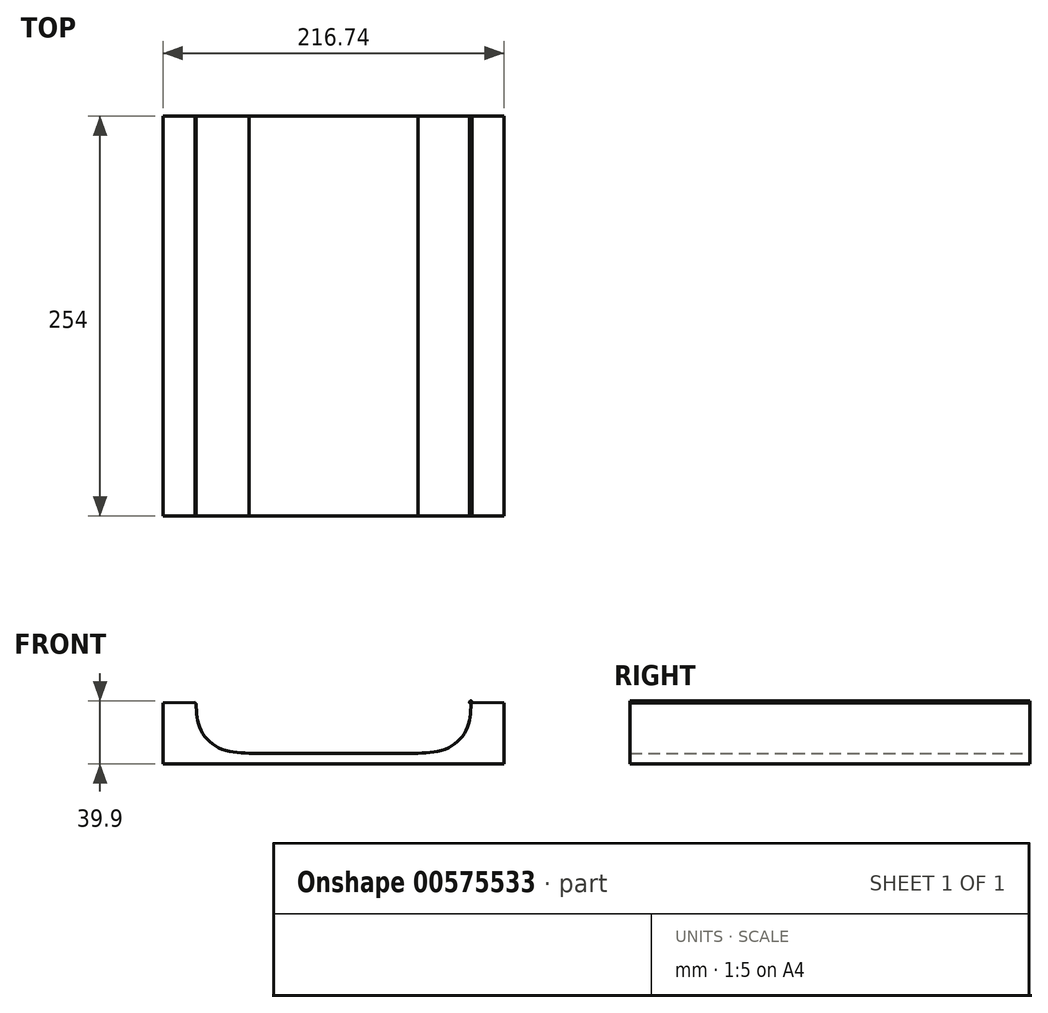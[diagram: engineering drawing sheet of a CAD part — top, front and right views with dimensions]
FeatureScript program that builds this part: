
annotation { "Feature Type Name" : "Feature", "Feature Type Description" : "" }
export const myFeature = defineFeature(function(context is Context, id is Id, definition is map)
    precondition{}
    {
        {
            var Q0;
            Q0=qCreatedBy(makeId("Front.planeOp"),FACE);
            var sketch = newSketch(context, id + "F0", { "sketchPlane" : qUnion([Q0])});
            skLineSegment(sketch, "E0.bottom", {"start": v(53.59, 3.32) * mm, "end": v(-53.59, 3.32) * mm});
            skLineSegment(sketch, "E0.top", {"start": v(53.59, -3.32) * mm, "end": v(-53.59, -3.32) * mm});
            skLineSegment(sketch, "E0.left", {"start": v(53.59, 3.32) * mm, "end": v(53.59, -3.32) * mm});
            skLineSegment(sketch, "E0.right", {"start": v(-53.59, 3.32) * mm, "end": v(-53.59, -3.32) * mm});
            skPoint(sketch, "E0.middle", {"position": v(0, 0) * mm});
            skFitSpline(sketch, "E1", {"points": [v(-53.59, 3.32) * mm, v(-73.74, 7.25) * mm, v(-85.05, 20.03) * mm, v(-87.26, 35.76) * mm], "startDerivative": vector(-60.33, 3.9) * mm, "endDerivative": vector(-1.15, 50.99) * mm});
            skFitSpline(sketch, "E2.MirrorCS", {"points": [v(53.59, 3.32) * mm, v(73.74, 7.25) * mm, v(85.05, 20.03) * mm, v(87.26, 35.76) * mm], "startDerivative": vector(60.33, 3.9) * mm, "endDerivative": vector(1.15, 50.99) * mm});
            skFitSpline(sketch, "E3.0", {"points": [v(54, -3.02) * mm, v(55.25, -2.94) * mm, v(57.81, -2.77) * mm, v(61.75, -2.43) * mm, v(65.75, -1.9) * mm, v(69.11, -1.2) * mm, v(71.8, -0.42) * mm, v(73.8, 0.29) * mm, v(75.78, 1.14) * mm, v(77.73, 2.16) * mm, v(79.56, 3.32) * mm, v(81.87, 5.02) * mm, v(84.48, 7.42) * mm, v(86.72, 10.1) * mm, v(88.27, 12.39) * mm, v(89.32, 14.16) * mm, v(90.1, 15.68) * mm, v(90.64, 16.93) * mm, v(91.16, 18.19) * mm, v(91.7, 19.77) * mm, v(92.4, 22.28) * mm, v(93, 25.37) * mm, v(93.5, 30.14) * mm, v(93.56, 33.5) * mm, v(93.6, 35.62) * mm]});
            skFitSpline(sketch, "E4.MirrorCS", {"points": [v(-53.59, 3.32) * mm, v(-73.74, 7.25) * mm, v(-85.05, 20.03) * mm, v(-87.26, 35.76) * mm], "startDerivative": vector(-60.33, 3.9) * mm, "endDerivative": vector(-1.15, 50.99) * mm});
            skFitSpline(sketch, "E5.0", {"points": [v(-54, -3.02) * mm, v(-55.25, -2.94) * mm, v(-57.81, -2.77) * mm, v(-61.75, -2.43) * mm, v(-65.75, -1.9) * mm, v(-69.11, -1.2) * mm, v(-71.8, -0.42) * mm, v(-73.8, 0.29) * mm, v(-75.78, 1.14) * mm, v(-77.73, 2.16) * mm, v(-79.56, 3.32) * mm, v(-81.87, 5.02) * mm, v(-84.48, 7.42) * mm, v(-86.72, 10.1) * mm, v(-88.27, 12.39) * mm, v(-89.32, 14.16) * mm, v(-90.1, 15.68) * mm, v(-90.64, 16.93) * mm, v(-91.16, 18.19) * mm, v(-91.7, 19.77) * mm, v(-92.4, 22.28) * mm, v(-93, 25.37) * mm, v(-93.5, 30.14) * mm, v(-93.56, 33.5) * mm, v(-93.6, 35.62) * mm]});
            skLineSegment(sketch, "E6", {"start": v(-93.6, 35.62) * mm, "end": v(-87.26, 35.76) * mm});
            skLineSegment(sketch, "E7", {"start": v(87.26, 35.76) * mm, "end": v(93.6, 35.62) * mm});
            skCircle(sketch, "E8", {"center": v(-87.26, 35.76) * mm, "radius": 0.81 * mm});
            skCircle(sketch, "E9.MirrorC", {"center": v(87.26, 35.76) * mm, "radius": 0.81 * mm});
            skLineSegment(sketch, "E10", {"start": v(-93.6, 35.62) * mm, "end": v(-109.54, 35.26) * mm});
            skLineSegment(sketch, "E11", {"start": v(-53.59, -3.32) * mm, "end": v(-108.37, -3.32) * mm});
            skLineSegment(sketch, "E12", {"start": v(-108.37, -3.32) * mm, "end": v(-108.37, 35.29) * mm});
            skLineSegment(sketch, "E13.MirrorCS", {"start": v(93.6, 35.62) * mm, "end": v(109.54, 35.26) * mm});
            skLineSegment(sketch, "E14.MirrorCS", {"start": v(108.37, -3.32) * mm, "end": v(108.37, 35.29) * mm});
            skLineSegment(sketch, "E15.MirrorCS", {"start": v(53.59, -3.32) * mm, "end": v(108.37, -3.32) * mm});
            skSolve(sketch);
        }
        {
            var Q0;
            {var subQ5=sQuery(id+"F0.wireOp",EDGE,"E0.right");Q0=makeQuery(id+"F0.imprint","IMPRINT",FACE,{"disambiguationData":[TD([[makeQuery(id+"F0.imprint","IMPRINT",EDGE,{"derivedFrom":subQ5}),-1.0]])]});}
            var Q1;
            {var subQ7=sQuery(id+"F0.wireOp",EDGE,"E0.left");Q1=makeQuery(id+"F0.imprint","IMPRINT",FACE,{"disambiguationData":[TD([[makeQuery(id+"F0.imprint","IMPRINT",EDGE,{"derivedFrom":subQ7}),1.0]])]});}
            var Q2;
            Q2=makeQuery(id+"F0.imprint","IMPRINT",FACE,{"disambiguationData":[TD([[makeQuery(id+"F0.imprint","IMPRINT",EDGE,{"derivedFrom":sQuery(id+"F0.wireOp",EDGE,"E0.bottom")}),1.0]])]});
            var Q3;
            {var subQ0=sQuery(id+"F0.wireOp",EDGE,"E6");var subQ1=sQuery(id+"F0.wireOp",EDGE,"E4.MirrorCS");var subQ2=makeQuery(id+"F0.imprint","INTERSECT",VERTEX,{"derivedFrom":[subQ1,subQ0]});Q3=makeQuery(id+"F0.imprint","IMPRINT",FACE,{"disambiguationData":[TD([[makeQuery(id+"F0.imprint","IMPRINT",EDGE,{"disambiguationData":[TD([[subQ2,1.0]])],"derivedFrom":subQ1}),-1.0]])]});}
            var Q4;
            {var subQ0=sQuery(id+"F0.wireOp",EDGE,"E6");var subQ1=sQuery(id+"F0.wireOp",EDGE,"E4.MirrorCS");var subQ2=makeQuery(id+"F0.imprint","INTERSECT",VERTEX,{"derivedFrom":[subQ1,subQ0]});Q4=makeQuery(id+"F0.imprint","IMPRINT",FACE,{"disambiguationData":[TD([[makeQuery(id+"F0.imprint","IMPRINT",EDGE,{"disambiguationData":[TD([[subQ2,1.0]])],"derivedFrom":subQ1}),1.0]])]});}
            var Q5;
            {var subQ0=sQuery(id+"F0.wireOp",EDGE,"E7");var subQ1=sQuery(id+"F0.wireOp",EDGE,"E2.MirrorCS");var subQ2=makeQuery(id+"F0.imprint","INTERSECT",VERTEX,{"derivedFrom":[subQ1,subQ0]});Q5=makeQuery(id+"F0.imprint","IMPRINT",FACE,{"disambiguationData":[TD([[makeQuery(id+"F0.imprint","IMPRINT",EDGE,{"disambiguationData":[TD([[subQ2,1.0]])],"derivedFrom":subQ1}),-1.0]])]});}
            var Q6;
            {var subQ0=sQuery(id+"F0.wireOp",EDGE,"E7");var subQ1=sQuery(id+"F0.wireOp",EDGE,"E2.MirrorCS");var subQ2=makeQuery(id+"F0.imprint","INTERSECT",VERTEX,{"derivedFrom":[subQ1,subQ0]});Q6=makeQuery(id+"F0.imprint","IMPRINT",FACE,{"disambiguationData":[TD([[makeQuery(id+"F0.imprint","IMPRINT",EDGE,{"disambiguationData":[TD([[subQ2,1.0]])],"derivedFrom":subQ1}),1.0]])]});}
            extrude(context, id + "F1", {"entities" : qUnion([Q0, Q1, Q2, Q3, Q4, Q5, Q6]), "depth" : 254 * mm, "offsetDistance" : 25.4 * mm});
        }
    });
